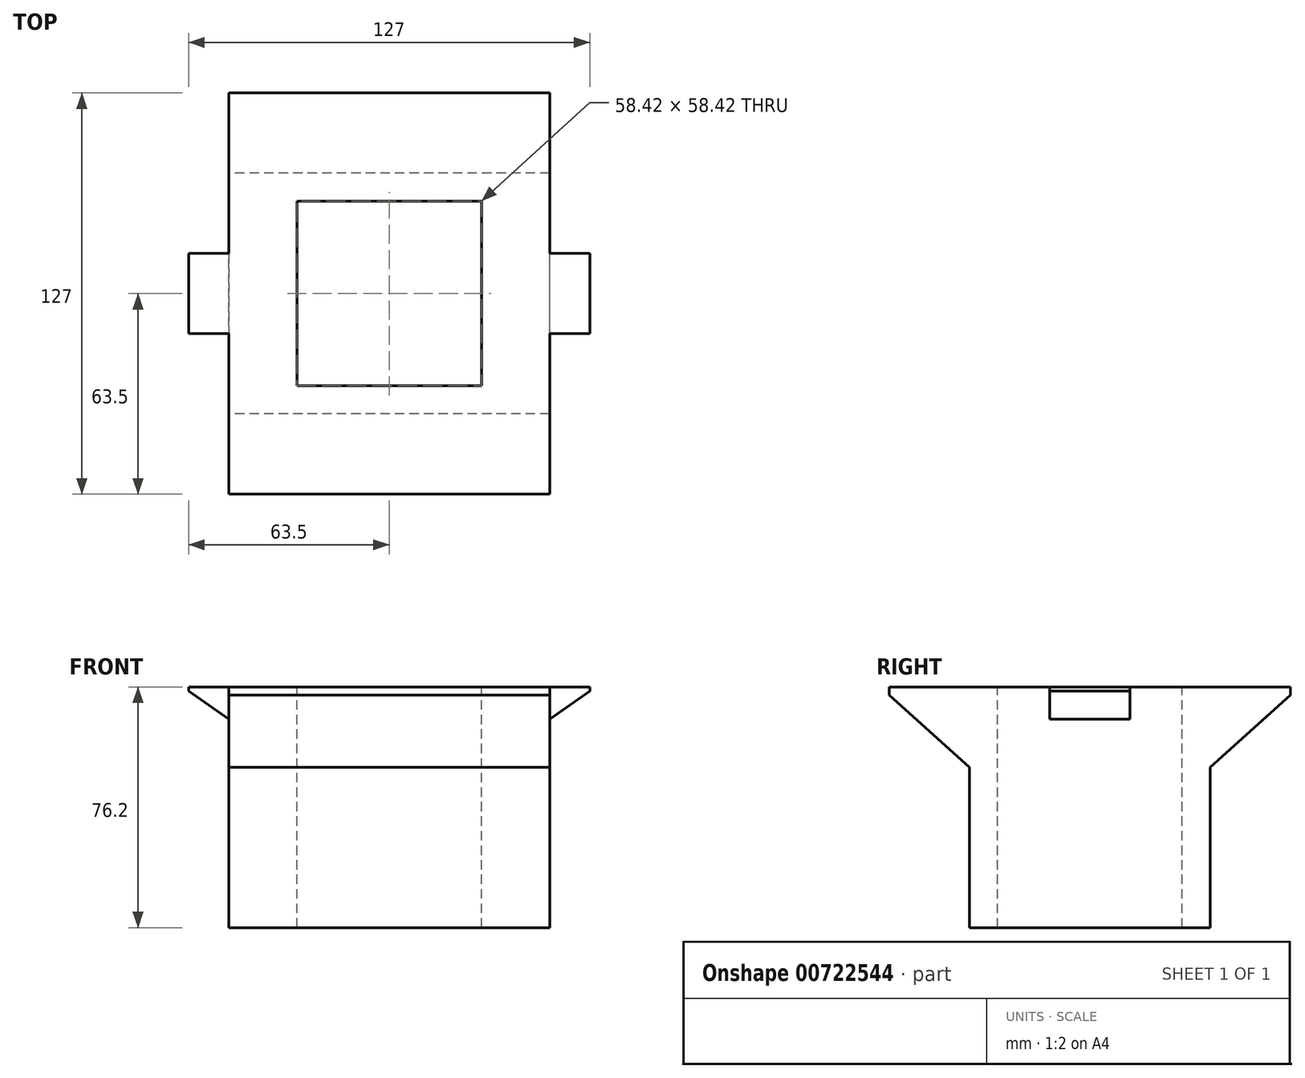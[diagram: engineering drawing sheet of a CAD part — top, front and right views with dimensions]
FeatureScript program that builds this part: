
annotation { "Feature Type Name" : "Feature", "Feature Type Description" : "" }
export const myFeature = defineFeature(function(context is Context, id is Id, definition is map)
    precondition{}
    {
        {
            var Q0;
            Q0=qCreatedBy(makeId("Top.planeOp"),FACE);
            var sketch = newSketch(context, id + "F0", { "sketchPlane" : qUnion([Q0])});
            skLineSegment(sketch, "E0.bottom", {"start": v(50.8, -38.1) * mm, "end": v(-50.8, -38.1) * mm});
            skLineSegment(sketch, "E0.top", {"start": v(50.8, 38.1) * mm, "end": v(-50.8, 38.1) * mm});
            skLineSegment(sketch, "E0.left", {"start": v(50.8, -38.1) * mm, "end": v(50.8, 38.1) * mm});
            skLineSegment(sketch, "E0.right", {"start": v(-50.8, -38.1) * mm, "end": v(-50.8, 38.1) * mm});
            skPoint(sketch, "E0.middle", {"position": v(0, 0) * mm});
            skSolve(sketch);
        }
        {
            var Q0;
            Q0=makeQuery(id+"F0.imprint","IMPRINT",FACE,{"disambiguationData":[TD([[makeQuery(id+"F0.imprint","IMPRINT",EDGE,{"derivedFrom":sQuery(id+"F0.wireOp",EDGE,"E0.bottom")}),-1.0]])]});
            extrude(context, id + "F1", {"entities" : qUnion([Q0]), "depth" : 76.2 * mm, "offsetDistance" : 25.4 * mm});
        }
        {
            var Q0;
            Q0=makeQuery(id+"F1.opExtrude","CAP_FACE",FACE,{"disambiguationData":[OSD([sQuery(id+"F0.wireOp",EDGE,"E0.bottom"),sQuery(id+"F0.wireOp",EDGE,"E0.top"),sQuery(id+"F0.wireOp",EDGE,"E0.left"),sQuery(id+"F0.wireOp",EDGE,"E0.right")])],"isStart":false});
            var sketch = newSketch(context, id + "F2", { "sketchPlane" : qUnion([Q0])});
            skLineSegment(sketch, "E1.bottom", {"start": v(29.21, -29.2) * mm, "end": v(-29.21, -29.21) * mm});
            skLineSegment(sketch, "E1.top", {"start": v(29.21, 29.21) * mm, "end": v(-29.2, 29.21) * mm});
            skLineSegment(sketch, "E1.left", {"start": v(29.21, -29.2) * mm, "end": v(29.21, 29.21) * mm});
            skLineSegment(sketch, "E1.right", {"start": v(-29.21, -29.21) * mm, "end": v(-29.2, 29.21) * mm});
            skPoint(sketch, "E1.middle", {"position": v(0, 0) * mm});
            skSolve(sketch);
        }
        {
            var Q0;
            Q0=makeQuery(id+"F2.imprint","IMPRINT",FACE,{"disambiguationData":[TD([[makeQuery(id+"F2.imprint","IMPRINT",EDGE,{"derivedFrom":sQuery(id+"F2.wireOp",EDGE,"E1.bottom")}),-1.0]])]});
            extrude(context, id + "F3", {"entities" : qUnion([Q0]), "operationType" : NewBodyOperationType.REMOVE, "oppositeDirection" : true, "depth" : 228.6 * mm, "offsetDistance" : 25.4 * mm});
        }
        {
            var Q0;
            Q0=makeQuery(id+"F1.opExtrude","SWEPT_FACE",FACE,{"disambiguationData":[OSD([sQuery(id+"F0.wireOp",EDGE,"E0.top")])]});
            var sketch = newSketch(context, id + "F4", { "sketchPlane" : qUnion([Q0])});
            skLineSegment(sketch, "E2.bottom", {"start": v(-50.8, 76.2) * mm, "end": v(50.8, 76.2) * mm});
            skLineSegment(sketch, "E2.top", {"start": v(-50.8, 50.8) * mm, "end": v(50.8, 50.8) * mm});
            skLineSegment(sketch, "E2.left", {"start": v(-50.8, 76.2) * mm, "end": v(-50.8, 50.8) * mm});
            skLineSegment(sketch, "E2.right", {"start": v(50.8, 76.2) * mm, "end": v(50.8, 50.8) * mm});
            skSolve(sketch);
        }
        {
            var Q0;
            Q0=makeQuery(id+"F4.imprint","IMPRINT",FACE,{"disambiguationData":[TD([[makeQuery(id+"F4.imprint","IMPRINT",EDGE,{"derivedFrom":sQuery(id+"F4.wireOp",EDGE,"E2.bottom")}),-1.0]])]});
            extrude(context, id + "F5", {"entities" : qUnion([Q0]), "operationType" : NewBodyOperationType.ADD, "depth" : 25.4 * mm, "offsetDistance" : 25.4 * mm});
        }
        {
            var Q0;
            Q0=makeQuery(id+"F1.opExtrude","SWEPT_FACE",FACE,{"disambiguationData":[OSD([sQuery(id+"F0.wireOp",EDGE,"E0.bottom")])]});
            var sketch = newSketch(context, id + "F6", { "sketchPlane" : qUnion([Q0])});
            skLineSegment(sketch, "E3.bottom", {"start": v(-50.8, 76.2) * mm, "end": v(50.8, 76.2) * mm});
            skLineSegment(sketch, "E3.top", {"start": v(-50.8, 50.8) * mm, "end": v(50.8, 50.8) * mm});
            skLineSegment(sketch, "E3.left", {"start": v(-50.8, 76.2) * mm, "end": v(-50.8, 50.8) * mm});
            skLineSegment(sketch, "E3.right", {"start": v(50.8, 76.2) * mm, "end": v(50.8, 50.8) * mm});
            skSolve(sketch);
        }
        {
            var Q0;
            Q0=makeQuery(id+"F6.imprint","IMPRINT",FACE,{"disambiguationData":[TD([[makeQuery(id+"F6.imprint","IMPRINT",EDGE,{"derivedFrom":sQuery(id+"F6.wireOp",EDGE,"E3.bottom")}),1.0]])]});
            extrude(context, id + "F7", {"entities" : qUnion([Q0]), "operationType" : NewBodyOperationType.ADD, "depth" : 25.4 * mm, "offsetDistance" : 25.4 * mm});
        }
        {
            var Q0;
            Q0=makeQuery(id+"F7.boolean.opBoolean","MERGE",FACE,{"derivedFrom":[makeQuery(id+"F5.boolean.opBoolean","MERGE",FACE,{"derivedFrom":[makeQuery(id+"F1.opExtrude","SWEPT_FACE",FACE,{"disambiguationData":[OSD([sQuery(id+"F0.wireOp",EDGE,"E0.left")])]}),makeQuery(id+"F5.opExtrude","SWEPT_FACE",FACE,{"disambiguationData":[OSD([sQuery(id+"F4.wireOp",EDGE,"E2.left")])]})]}),makeQuery(id+"F7.opExtrude","SWEPT_FACE",FACE,{"disambiguationData":[OSD([sQuery(id+"F6.wireOp",EDGE,"E3.right")])]})]});
            var sketch = newSketch(context, id + "F8", { "sketchPlane" : qUnion([Q0])});
            skLineSegment(sketch, "E4", {"start": v(-63.5, 76.2) * mm, "end": v(-63.5, 73.66) * mm});
            skLineSegment(sketch, "E5", {"start": v(-63.5, 73.66) * mm, "end": v(-38.1, 50.8) * mm});
            skLineSegment(sketch, "E6", {"start": v(63.5, 76.2) * mm, "end": v(63.5, 73.66) * mm});
            skLineSegment(sketch, "E7", {"start": v(63.5, 73.66) * mm, "end": v(38.1, 50.8) * mm});
            skSolve(sketch);
        }
        {
            var Q0;
            {var subQ0=sQuery(id+"F8.wireOp",EDGE,"E5");Q0=makeQuery(id+"F8.imprint","IMPRINT",FACE,{"disambiguationData":[TD([[makeQuery(id+"F8.imprint","IMPRINT",EDGE,{"derivedFrom":subQ0}),-1.0]])]});}
            var Q1;
            {var subQ0=sQuery(id+"F8.wireOp",EDGE,"E7");Q1=makeQuery(id+"F8.imprint","IMPRINT",FACE,{"disambiguationData":[TD([[makeQuery(id+"F8.imprint","IMPRINT",EDGE,{"derivedFrom":subQ0}),1.0]])]});}
            extrude(context, id + "F9", {"entities" : qUnion([Q0, Q1]), "operationType" : NewBodyOperationType.REMOVE, "oppositeDirection" : true, "depth" : 228.6 * mm, "offsetDistance" : 25.4 * mm});
        }
        {
            var Q0;
            Q0=makeQuery(id+"F7.boolean.opBoolean","MERGE",FACE,{"derivedFrom":[makeQuery(id+"F5.boolean.opBoolean","MERGE",FACE,{"derivedFrom":[makeQuery(id+"F1.opExtrude","SWEPT_FACE",FACE,{"disambiguationData":[OSD([sQuery(id+"F0.wireOp",EDGE,"E0.left")])]}),makeQuery(id+"F5.opExtrude","SWEPT_FACE",FACE,{"disambiguationData":[OSD([sQuery(id+"F4.wireOp",EDGE,"E2.left")])]})]}),makeQuery(id+"F7.opExtrude","SWEPT_FACE",FACE,{"disambiguationData":[OSD([sQuery(id+"F6.wireOp",EDGE,"E3.right")])]})]});
            var sketch = newSketch(context, id + "F10", { "sketchPlane" : qUnion([Q0])});
            skLineSegment(sketch, "E8", {"start": v(-63.5, 76.2) * mm, "end": v(-12.7, 76.2) * mm});
            skLineSegment(sketch, "E9", {"start": v(-12.7, 76.2) * mm, "end": v(-12.7, 66.04) * mm});
            skLineSegment(sketch, "E10", {"start": v(-12.7, 66.04) * mm, "end": v(12.7, 66.04) * mm});
            skLineSegment(sketch, "E11", {"start": v(12.7, 66.04) * mm, "end": v(12.7, 76.2) * mm});
            skSolve(sketch);
        }
        {
            var Q0;
            Q0 = qSketchRegion(id + "F10", true);
            var Q1;
            {var subQ0=sQuery(id+"F10.wireOp",EDGE,"E9");Q1=makeQuery(id+"F10.imprint","IMPRINT",FACE,{"disambiguationData":[TD([[makeQuery(id+"F10.imprint","IMPRINT",EDGE,{"derivedFrom":subQ0}),1.0]])]});}
            extrude(context, id + "F11", {"entities" : qUnion([Q0, Q1]), "operationType" : NewBodyOperationType.ADD, "depth" : 12.7 * mm, "offsetDistance" : 25.4 * mm});
        }
        {
            var Q0;
            Q0=makeQuery(id+"F11.opExtrude","SWEPT_FACE",FACE,{"disambiguationData":[OSD([sQuery(id+"F10.wireOp",EDGE,"E9")])]});
            var sketch = newSketch(context, id + "F12", { "sketchPlane" : qUnion([Q0])});
            skLineSegment(sketch, "E12", {"start": v(63.5, 76.2) * mm, "end": v(63.5, 74.93) * mm});
            skLineSegment(sketch, "E13", {"start": v(63.5, 74.93) * mm, "end": v(50.8, 66.04) * mm});
            skSolve(sketch);
        }
        {
            var Q0;
            {var subQ0=sQuery(id+"F12.wireOp",EDGE,"E13");Q0=makeQuery(id+"F12.imprint","IMPRINT",FACE,{"disambiguationData":[TD([[makeQuery(id+"F12.imprint","IMPRINT",EDGE,{"derivedFrom":subQ0}),1.0]])]});}
            extrude(context, id + "F13", {"entities" : qUnion([Q0]), "operationType" : NewBodyOperationType.REMOVE, "oppositeDirection" : true, "depth" : 228.6 * mm, "offsetDistance" : 25.4 * mm});
        }
        {
            var Q0;
            Q0=makeQuery(id+"F7.boolean.opBoolean","MERGE",FACE,{"derivedFrom":[makeQuery(id+"F5.boolean.opBoolean","MERGE",FACE,{"derivedFrom":[makeQuery(id+"F1.opExtrude","SWEPT_FACE",FACE,{"disambiguationData":[OSD([sQuery(id+"F0.wireOp",EDGE,"E0.right")])]}),makeQuery(id+"F5.opExtrude","SWEPT_FACE",FACE,{"disambiguationData":[OSD([sQuery(id+"F4.wireOp",EDGE,"E2.right")])]})]}),makeQuery(id+"F7.opExtrude","SWEPT_FACE",FACE,{"disambiguationData":[OSD([sQuery(id+"F6.wireOp",EDGE,"E3.left")])]})]});
            var sketch = newSketch(context, id + "F14", { "sketchPlane" : qUnion([Q0])});
            skLineSegment(sketch, "E14", {"start": v(-63.5, 76.2) * mm, "end": v(-12.7, 76.2) * mm});
            skLineSegment(sketch, "E15", {"start": v(-12.7, 76.2) * mm, "end": v(-12.7, 66.04) * mm});
            skLineSegment(sketch, "E16", {"start": v(-12.7, 66.04) * mm, "end": v(12.7, 66.04) * mm});
            skLineSegment(sketch, "E17", {"start": v(12.7, 66.04) * mm, "end": v(12.7, 76.2) * mm});
            skSolve(sketch);
        }
        {
            var Q0;
            {var subQ0=sQuery(id+"F14.wireOp",EDGE,"E15");Q0=makeQuery(id+"F14.imprint","IMPRINT",FACE,{"disambiguationData":[TD([[makeQuery(id+"F14.imprint","IMPRINT",EDGE,{"derivedFrom":subQ0}),1.0]])]});}
            extrude(context, id + "F15", {"entities" : qUnion([Q0]), "operationType" : NewBodyOperationType.ADD, "depth" : 12.7 * mm, "offsetDistance" : 25.4 * mm});
        }
        {
            var Q0;
            Q0=makeQuery(id+"F15.opExtrude","SWEPT_FACE",FACE,{"disambiguationData":[OSD([sQuery(id+"F14.wireOp",EDGE,"E15")])]});
            var sketch = newSketch(context, id + "F16", { "sketchPlane" : qUnion([Q0])});
            skLineSegment(sketch, "E18", {"start": v(63.5, 76.2) * mm, "end": v(63.5, 74.93) * mm});
            skLineSegment(sketch, "E19", {"start": v(63.5, 74.93) * mm, "end": v(50.8, 66.04) * mm});
            skSolve(sketch);
        }
        {
            var Q0;
            {var subQ0=sQuery(id+"F16.wireOp",EDGE,"E19");Q0=makeQuery(id+"F16.imprint","IMPRINT",FACE,{"disambiguationData":[TD([[makeQuery(id+"F16.imprint","IMPRINT",EDGE,{"derivedFrom":subQ0}),1.0]])]});}
            extrude(context, id + "F17", {"entities" : qUnion([Q0]), "operationType" : NewBodyOperationType.REMOVE, "oppositeDirection" : true, "depth" : 228.6 * mm, "offsetDistance" : 25.4 * mm});
        }
    });
